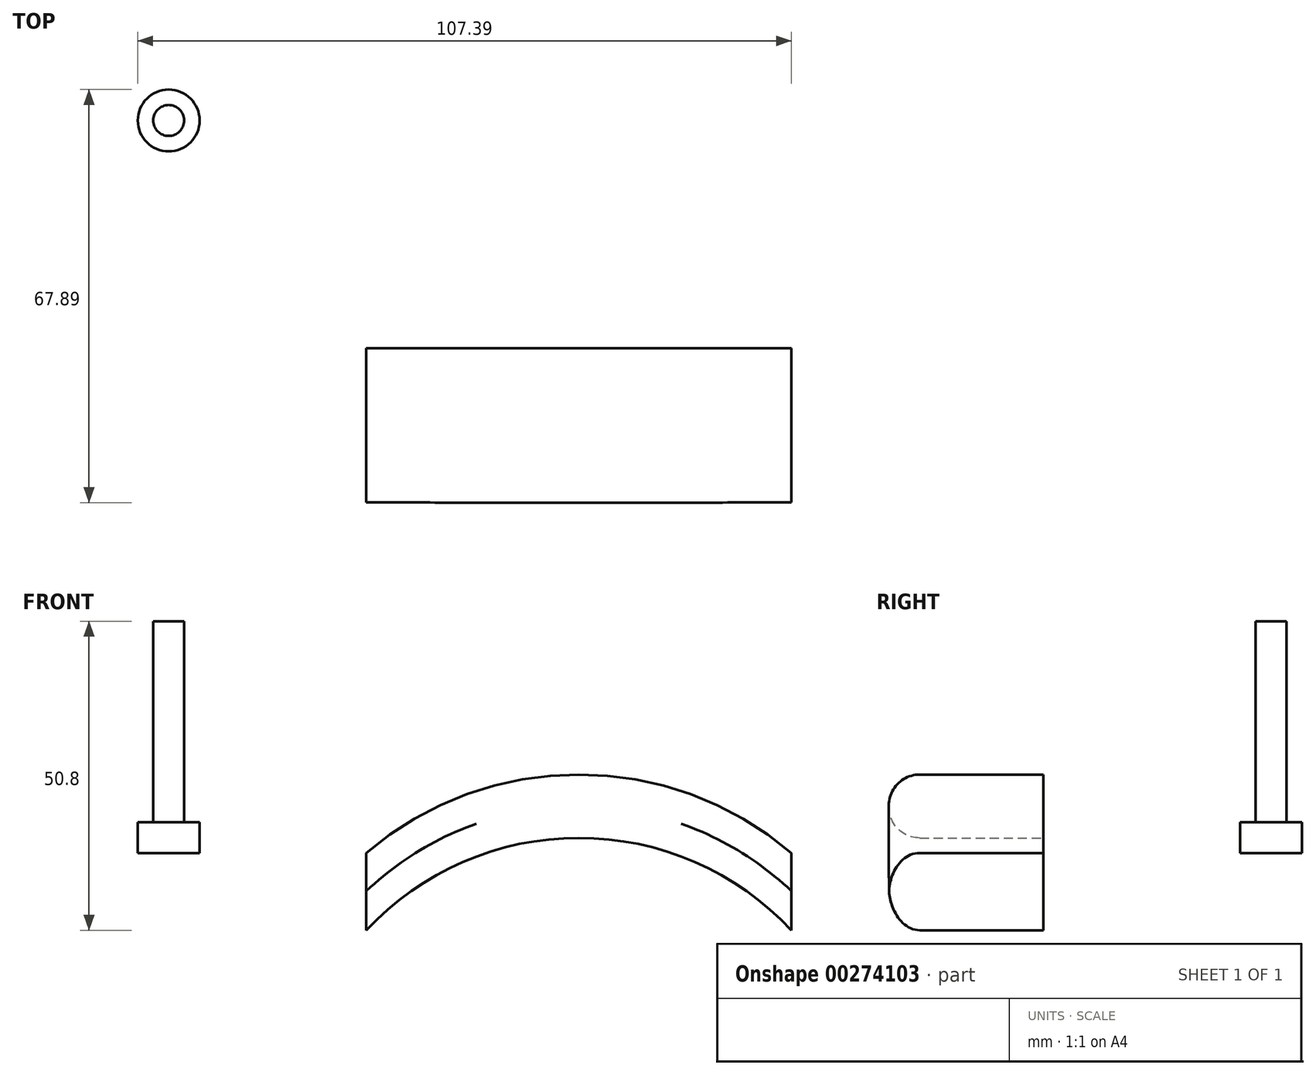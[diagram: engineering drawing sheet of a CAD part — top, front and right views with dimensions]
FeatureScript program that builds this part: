
annotation { "Feature Type Name" : "Feature", "Feature Type Description" : "" }
export const myFeature = defineFeature(function(context is Context, id is Id, definition is map)
    precondition{}
    {
        {
            var Q0;
            Q0=qCreatedBy(makeId("Front.planeOp"),FACE);
            var sketch = newSketch(context, id + "F0", { "sketchPlane" : qUnion([Q0])});
            skArc(sketch, "E0", {"start": v(36.34, 0) * mm, "mid": v(1.41, 12.89) * mm, "end": v(-33.51, 0) * mm});
            skArc(sketch, "E1", {"start": v(36.34, -12.7) * mm, "mid": v(1.41, 2.48) * mm, "end": v(-33.51, -12.7) * mm});
            skLineSegment(sketch, "E2", {"start": v(-33.51, 0) * mm, "end": v(-33.51, -12.7) * mm});
            skLineSegment(sketch, "E3", {"start": v(36.34, 0) * mm, "end": v(36.34, -12.7) * mm});
            skSolve(sketch);
        }
        {
            var Q0;
            Q0=makeQuery(id+"F0.imprint","IMPRINT",FACE,{"disambiguationData":[TD([[makeQuery(id+"F0.imprint","IMPRINT",EDGE,{"derivedFrom":sQuery(id+"F0.wireOp",EDGE,"E0")}),1.0]])]});
            extrude(context, id + "F1", {"entities" : qUnion([Q0]), "depth" : 25.4 * mm});
        }
        {
            var Q0;
            Q0=makeQuery(id+"F1.opExtrude","CAP_EDGE",EDGE,{"disambiguationData":[OSD([sQuery(id+"F0.wireOp",EDGE,"E0")])],"isStart":false});
            var Q1;
            Q1=makeQuery(id+"F1.opExtrude","CAP_EDGE",EDGE,{"disambiguationData":[OSD([sQuery(id+"F0.wireOp",EDGE,"E1")])],"isStart":false});
            fillet(context, id + "F2", {"entities" : qUnion([Q0, Q1]), "radius" : 5.08 * mm, "tangentPropagation" : true, "allowEdgeOverflow" : false});
        }
        {
            var Q0;
            Q0=qCreatedBy(makeId("Top.planeOp"),FACE);
            var sketch = newSketch(context, id + "F3", { "sketchPlane" : qUnion([Q0])});
            skCircle(sketch, "E4", {"center": v(-65.97, 37.41) * mm, "radius": 2.54 * mm});
            skCircle(sketch, "E5", {"center": v(-65.97, 37.41) * mm, "radius": 5.08 * mm});
            skSolve(sketch);
        }
        {
            var Q0;
            Q0=makeQuery(id+"F3.imprint","IMPRINT",FACE,{"disambiguationData":[TD([[makeQuery(id+"F3.imprint","IMPRINT",EDGE,{"derivedFrom":sQuery(id+"F3.wireOp",EDGE,"E4")}),1.0]])]});
            extrude(context, id + "F4", {"entities" : qUnion([Q0]), "depth" : 38.1 * mm});
        }
        {
            var Q0;
            Q0 = qSketchRegion(id + "F3", true);
            extrude(context, id + "F5", {"entities" : qUnion([Q0]), "operationType" : NewBodyOperationType.ADD, "depth" : 5.08 * mm});
        }
    });
